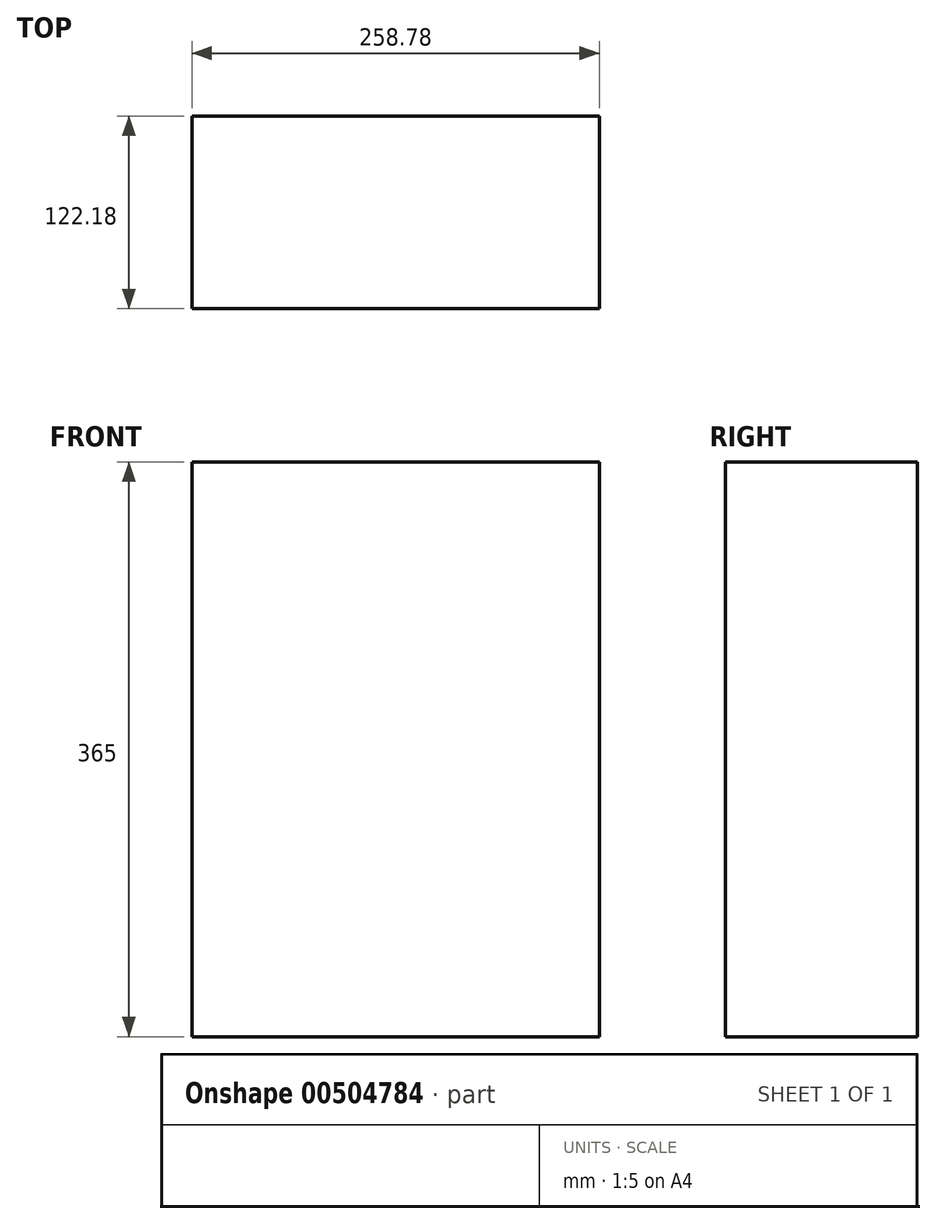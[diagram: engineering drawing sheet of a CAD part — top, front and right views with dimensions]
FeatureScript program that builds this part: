
annotation { "Feature Type Name" : "Feature", "Feature Type Description" : "" }
export const myFeature = defineFeature(function(context is Context, id is Id, definition is map)
    precondition{}
    {
        {
            var Q0;
            Q0=qCreatedBy(makeId("Top.planeOp"),FACE);
            var sketch = newSketch(context, id + "F0", { "sketchPlane" : qUnion([Q0])});
            skLineSegment(sketch, "E0", {"start": v(158.68, 243.19) * mm, "end": v(158.68, 121.01) * mm});
            skLineSegment(sketch, "E1", {"start": v(158.68, 121.01) * mm, "end": v(417.46, 121.01) * mm});
            skLineSegment(sketch, "E2", {"start": v(417.46, 121.01) * mm, "end": v(417.46, 243.19) * mm});
            skLineSegment(sketch, "E3", {"start": v(417.46, 243.19) * mm, "end": v(158.68, 243.19) * mm});
            skSolve(sketch);
        }
        {
            var Q0;
            Q0=makeQuery(id+"F0.imprint","IMPRINT",FACE,{"disambiguationData":[TD([[makeQuery(id+"F0.imprint","IMPRINT",EDGE,{"derivedFrom":sQuery(id+"F0.wireOp",EDGE,"E0")}),1.0]])]});
            extrude(context, id + "F1", {"entities" : qUnion([Q0]), "depth" : 365 * mm});
        }
    });
